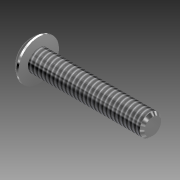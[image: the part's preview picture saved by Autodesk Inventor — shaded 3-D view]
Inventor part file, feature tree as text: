
AUTODESK INVENTOR PART (.ipt)
format: ipt  version: 2011 (Build 150239000, 239)  size: 112,128 bytes
history: native  units: in
note: dims shown in document units (in); Inventor stores cm internally (conversion verified against a paired STEP export)
features: other x1, imported_body x1, thread x1
ambient origin geometry x8: Origin, YZ Plane, XZ Plane, XY Plane, X Axis, Y Axis, Z Axis, Center Point
feature tree (3):
  parser-record x1  (decoder bookkeeping rows leaked as tree rows — omitted from the tree; the rows remain in map.json)
  imported_body  "Base1"
  thread  "Thread1"  [1 undecoded]
note: 1 required parameter value undecoded (feature->parameter linkage not recoverable at this tier; creation-order binding heuristic only, values carry confidence <= 0.55)
